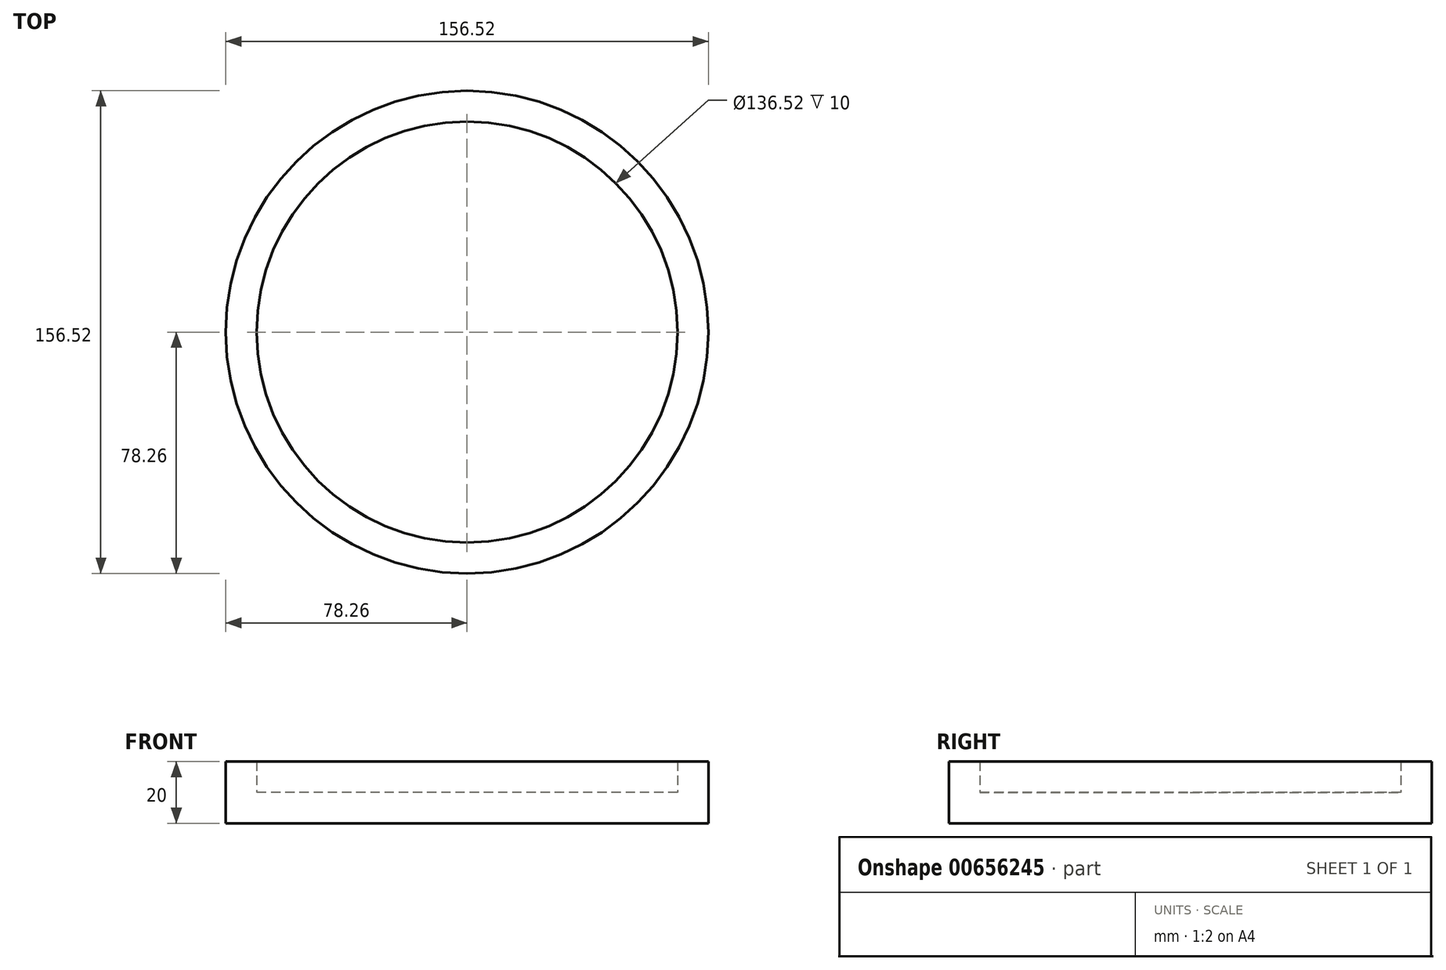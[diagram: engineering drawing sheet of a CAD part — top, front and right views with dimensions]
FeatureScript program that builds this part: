
annotation { "Feature Type Name" : "Feature", "Feature Type Description" : "" }
export const myFeature = defineFeature(function(context is Context, id is Id, definition is map)
    precondition{}
    {
        {
            var Q0;
            Q0=qCreatedBy(makeId("Top.planeOp"),FACE);
            var sketch = newSketch(context, id + "F0", { "sketchPlane" : qUnion([Q0])});
            skCircle(sketch, "E0", {"center": v(0, 0) * mm, "radius": 68.26 * mm});
            skSolve(sketch);
        }
        {
            var Q0;
            Q0=makeQuery(id+"F0.imprint","IMPRINT",FACE,{"disambiguationData":[TD([[makeQuery(id+"F0.imprint","IMPRINT",EDGE,{"derivedFrom":sQuery(id+"F0.wireOp",EDGE,"E0")}),1.0]])]});
            extrude(context, id + "F1", {"entities" : qUnion([Q0]), "depth" : 10 * mm, "offsetDistance" : 25.4 * mm});
        }
        {
            var Q0;
            Q0=makeQuery(id+"F1.opExtrude","CAP_FACE",FACE,{"disambiguationData":[OSD([sQuery(id+"F0.wireOp",EDGE,"E0")])],"isStart":false});
            var sketch = newSketch(context, id + "F2", { "sketchPlane" : qUnion([Q0])});
            skCircle(sketch, "E1", {"center": v(0, 0) * mm, "radius": 60.15 * mm});
            skSolve(sketch);
        }
        {
            var Q0;
            Q0=makeQuery(id+"F2.imprint","IMPRINT",FACE,{"disambiguationData":[TD([[makeQuery(id+"F2.imprint","IMPRINT",EDGE,{"derivedFrom":sQuery(id+"F2.wireOp",EDGE,"E1")}),1.0]])]});
            extrude(context, id + "F3", {"entities" : qUnion([Q0]), "operationType" : NewBodyOperationType.ADD, "oppositeDirection" : true, "depth" : 5 * mm, "offsetDistance" : 25.4 * mm});
        }
        {
            var Q0;
            Q0=makeQuery(id+"F1.opExtrude","CAP_FACE",FACE,{"disambiguationData":[OSD([sQuery(id+"F0.wireOp",EDGE,"E0")])],"isStart":false});
            var sketch = newSketch(context, id + "F4", { "sketchPlane" : qUnion([Q0])});
            skCircle(sketch, "E2", {"center": v(0, 0) * mm, "radius": 56.54 * mm});
            skSolve(sketch);
        }
        {
            var Q0;
            Q0=makeQuery(id+"F4.imprint","IMPRINT",FACE,{"disambiguationData":[TD([[makeQuery(id+"F4.imprint","IMPRINT",EDGE,{"derivedFrom":sQuery(id+"F4.wireOp",EDGE,"E2")}),1.0]])]});
            extrude(context, id + "F5", {"entities" : qUnion([Q0]), "operationType" : NewBodyOperationType.ADD, "oppositeDirection" : true, "depth" : 7 * mm, "offsetDistance" : 25.4 * mm});
        }
        {
            var Q0;
            Q0=makeQuery(id+"F1.opExtrude","CAP_FACE",FACE,{"disambiguationData":[OSD([sQuery(id+"F0.wireOp",EDGE,"E0")])],"isStart":false});
            shell(context, id + "F6", {"entities" : qUnion([Q0]), "thickness" : 10 * mm, "oppositeDirection" : true});
        }
    });
